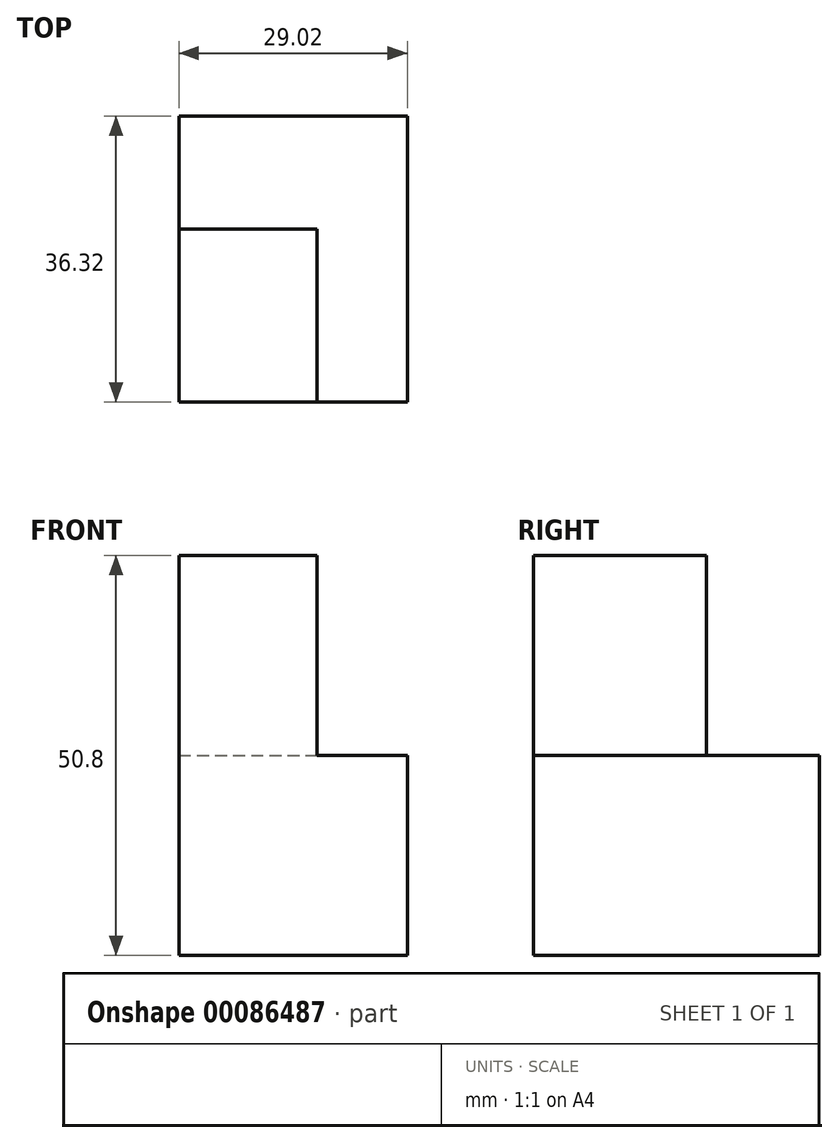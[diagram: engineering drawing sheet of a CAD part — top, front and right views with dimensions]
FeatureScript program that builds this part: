
annotation { "Feature Type Name" : "Feature", "Feature Type Description" : "" }
export const myFeature = defineFeature(function(context is Context, id is Id, definition is map)
    precondition{}
    {
        {
            var Q0;
            Q0=qCreatedBy(makeId("Top.planeOp"),FACE);
            var sketch = newSketch(context, id + "F0", { "sketchPlane" : qUnion([Q0])});
            skLineSegment(sketch, "E0.bottom", {"start": v(-14.5, -18.16) * mm, "end": v(14.5, -18.16) * mm});
            skLineSegment(sketch, "E0.top", {"start": v(-14.5, 18.16) * mm, "end": v(14.5, 18.16) * mm});
            skLineSegment(sketch, "E0.left", {"start": v(-14.5, -18.16) * mm, "end": v(-14.5, 18.16) * mm});
            skLineSegment(sketch, "E0.right", {"start": v(14.5, -18.16) * mm, "end": v(14.5, 18.16) * mm});
            skPoint(sketch, "E0.middle", {"position": v(0, 0) * mm});
            skSolve(sketch);
        }
        {
            var Q0;
            Q0 = qSketchRegion(id + "F0", true);
            extrude(context, id + "F1", {"entities" : qUnion([Q0]), "depth" : 25.4 * mm});
        }
        {
            var Q0;
            Q0=makeQuery(id+"F1.opExtrude","CAP_FACE",FACE,{"disambiguationData":[OSD([sQuery(id+"F0.wireOp",EDGE,"E0.bottom"),sQuery(id+"F0.wireOp",EDGE,"E0.top"),sQuery(id+"F0.wireOp",EDGE,"E0.left"),sQuery(id+"F0.wireOp",EDGE,"E0.right")])],"isStart":false});
            var sketch = newSketch(context, id + "F2", { "sketchPlane" : qUnion([Q0])});
            skLineSegment(sketch, "E1.bottom", {"start": v(-14.5, -18.16) * mm, "end": v(3.06, -18.16) * mm});
            skLineSegment(sketch, "E1.top", {"start": v(-14.5, 3.8) * mm, "end": v(3.06, 3.8) * mm});
            skLineSegment(sketch, "E1.left", {"start": v(-14.5, -18.16) * mm, "end": v(-14.5, 3.8) * mm});
            skLineSegment(sketch, "E1.right", {"start": v(3.06, -18.16) * mm, "end": v(3.06, 3.8) * mm});
            skSolve(sketch);
        }
        {
            var Q0;
            Q0 = qSketchRegion(id + "F2", true);
            extrude(context, id + "F3", {"entities" : qUnion([Q0]), "operationType" : NewBodyOperationType.ADD, "depth" : 25.4 * mm});
        }
    });
